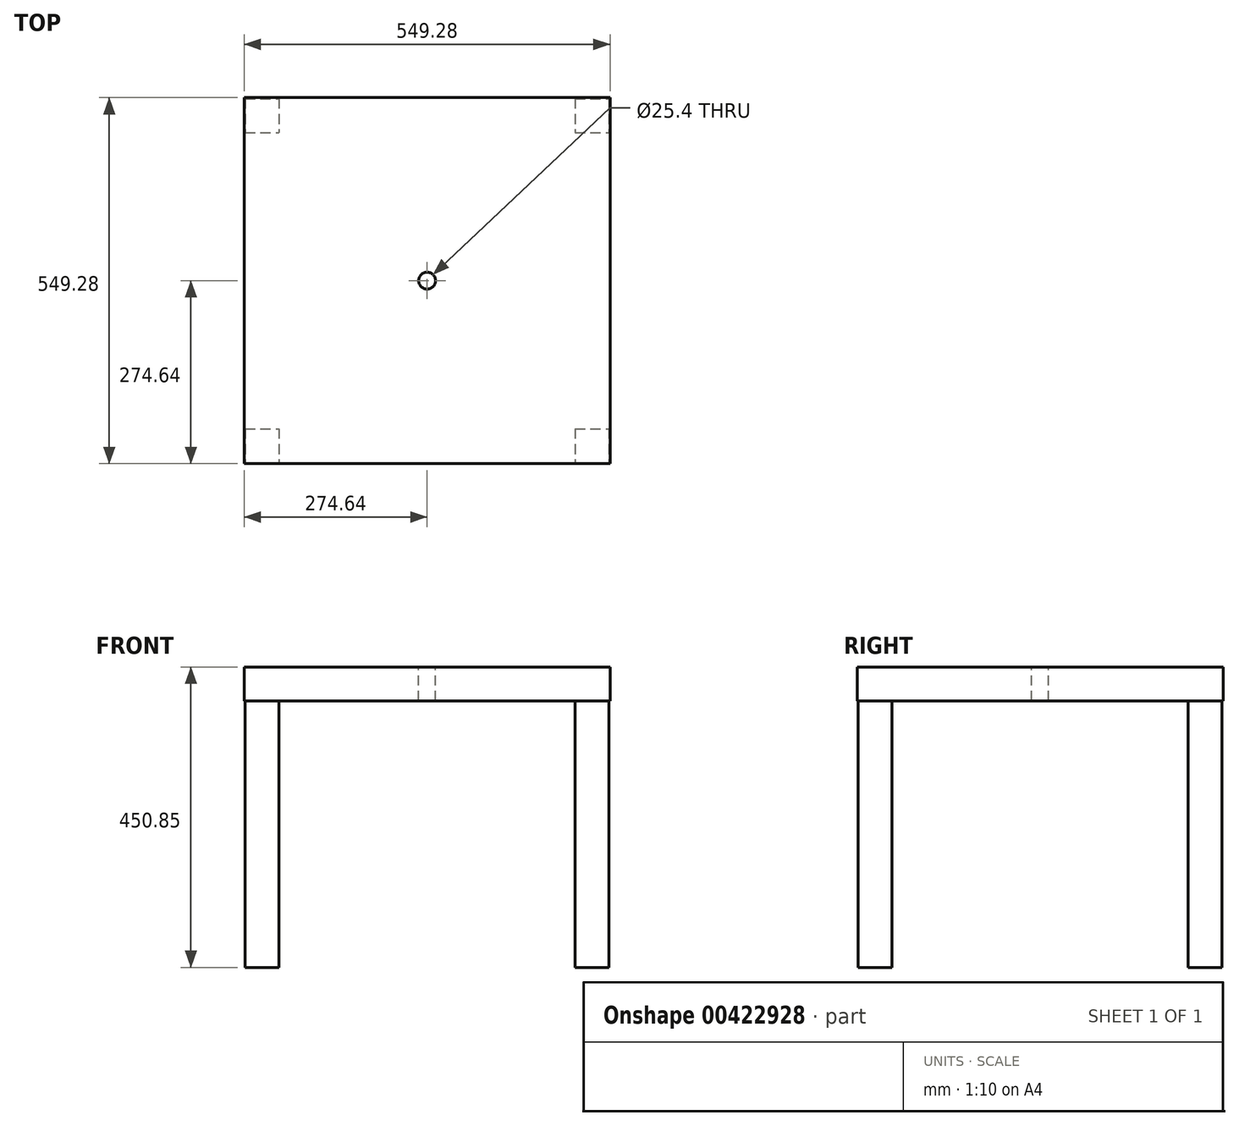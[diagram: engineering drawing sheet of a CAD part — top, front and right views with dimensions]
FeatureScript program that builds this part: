
annotation { "Feature Type Name" : "Feature", "Feature Type Description" : "" }
export const myFeature = defineFeature(function(context is Context, id is Id, definition is map)
    precondition{}
    {
        {
            var Q0;
            Q0=qCreatedBy(makeId("Top.planeOp"),FACE);
            var sketch = newSketch(context, id + "F0", { "sketchPlane" : qUnion([Q0])});
            skLineSegment(sketch, "E0.bottom", {"start": v(-273.05, 273.05) * mm, "end": v(-222.25, 273.05) * mm});
            skLineSegment(sketch, "E0.top", {"start": v(-273.05, 222.25) * mm, "end": v(-222.25, 222.25) * mm});
            skLineSegment(sketch, "E0.left", {"start": v(-273.05, 273.05) * mm, "end": v(-273.05, 222.25) * mm});
            skLineSegment(sketch, "E0.right", {"start": v(-222.25, 273.05) * mm, "end": v(-222.25, 222.25) * mm});
            skLineSegment(sketch, "E1.bottom", {"start": v(222.25, 273.05) * mm, "end": v(273.05, 273.05) * mm});
            skLineSegment(sketch, "E1.top", {"start": v(222.25, 222.25) * mm, "end": v(273.05, 222.25) * mm});
            skLineSegment(sketch, "E1.left", {"start": v(222.25, 273.05) * mm, "end": v(222.25, 222.25) * mm});
            skLineSegment(sketch, "E1.right", {"start": v(273.05, 273.05) * mm, "end": v(273.05, 222.25) * mm});
            skLineSegment(sketch, "E2.bottom", {"start": v(-273.05, -222.25) * mm, "end": v(-222.25, -222.25) * mm});
            skLineSegment(sketch, "E2.top", {"start": v(-273.05, -273.05) * mm, "end": v(-222.25, -273.05) * mm});
            skLineSegment(sketch, "E2.left", {"start": v(-273.05, -222.25) * mm, "end": v(-273.05, -273.05) * mm});
            skLineSegment(sketch, "E2.right", {"start": v(-222.25, -222.25) * mm, "end": v(-222.25, -273.05) * mm});
            skLineSegment(sketch, "E3.bottom", {"start": v(222.25, -222.25) * mm, "end": v(273.05, -222.25) * mm});
            skLineSegment(sketch, "E3.top", {"start": v(222.25, -273.05) * mm, "end": v(273.05, -273.05) * mm});
            skLineSegment(sketch, "E3.left", {"start": v(222.25, -222.25) * mm, "end": v(222.25, -273.05) * mm});
            skLineSegment(sketch, "E3.right", {"start": v(273.05, -222.25) * mm, "end": v(273.05, -273.05) * mm});
            skSolve(sketch);
        }
        {
            var Q0;
            Q0 = qSketchRegion(id + "F0", true);
            extrude(context, id + "F1", {"entities" : qUnion([Q0]), "depth" : 400.05 * mm});
        }
        {
            var Q0;
            Q0=makeQuery(id+"F1.opExtrude","CAP_FACE",FACE,{"disambiguationData":[OSD([sQuery(id+"F0.wireOp",EDGE,"E2.bottom"),sQuery(id+"F0.wireOp",EDGE,"E2.top"),sQuery(id+"F0.wireOp",EDGE,"E2.left"),sQuery(id+"F0.wireOp",EDGE,"E2.right")])],"isStart":false});
            var sketch = newSketch(context, id + "F2", { "sketchPlane" : qUnion([Q0])});
            skLineSegment(sketch, "E4.bottom", {"start": v(274.64, 274.64) * mm, "end": v(-274.64, 274.64) * mm});
            skLineSegment(sketch, "E4.top", {"start": v(274.64, -274.64) * mm, "end": v(-274.64, -274.64) * mm});
            skLineSegment(sketch, "E4.left", {"start": v(274.64, 274.64) * mm, "end": v(274.64, -274.64) * mm});
            skLineSegment(sketch, "E4.right", {"start": v(-274.64, 274.64) * mm, "end": v(-274.64, -274.64) * mm});
            skPoint(sketch, "E4.middle", {"position": v(0, 0) * mm});
            skSolve(sketch);
        }
        {
            var Q0;
            Q0=makeQuery(id+"F2.imprint","IMPRINT",FACE,{"disambiguationData":[TD([[makeQuery(id+"F2.imprint","IMPRINT",EDGE,{"derivedFrom":sQuery(id+"F2.wireOp",EDGE,"E4.bottom")}),1.0]])]});
            var Q1;
            Q1=makeQuery(id+"F2.imprint","IMPRINT",FACE,{"disambiguationData":[TD([[makeQuery(id+"F2.imprint","IMPRINT",EDGE,{"derivedFrom":makeQuery(id+"F1.opExtrude","CAP_EDGE",EDGE,{"disambiguationData":[OSD([sQuery(id+"F0.wireOp",EDGE,"E2.bottom")])],"isStart":false})}),-1.0]])]});
            extrude(context, id + "F3", {"entities" : qUnion([Q0, Q1]), "operationType" : NewBodyOperationType.ADD, "depth" : 50.8 * mm});
        }
        {
            var Q0;
            Q0=makeQuery(id+"F3.opExtrude","CAP_FACE",FACE,{"disambiguationData":[OSD([sQuery(id+"F2.wireOp",EDGE,"E4.bottom"),sQuery(id+"F2.wireOp",EDGE,"E4.top"),sQuery(id+"F2.wireOp",EDGE,"E4.left"),sQuery(id+"F2.wireOp",EDGE,"E4.right")])],"isStart":false});
            var sketch = newSketch(context, id + "F4", { "sketchPlane" : qUnion([Q0])});
            skCircle(sketch, "E5", {"center": v(0, 0) * mm, "radius": 12.7 * mm});
            skSolve(sketch);
        }
        {
            var Q0;
            Q0 = qSketchRegion(id + "F4", true);
            extrude(context, id + "F5", {"entities" : qUnion([Q0]), "operationType" : NewBodyOperationType.REMOVE, "endBound" : BoundingType.THROUGH_ALL, "oppositeDirection" : true, "depth" : 25.4 * mm});
        }
    });
